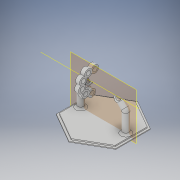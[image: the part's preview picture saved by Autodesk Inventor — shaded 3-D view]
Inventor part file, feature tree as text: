
AUTODESK INVENTOR PART (.ipt)
format: ipt  version: 2019 (Build 230136000, 136)  size: 253,952 bytes
history: native  units: mm
features: sketch x5, extrude x5, revolve x1, other x1, sweep x1, plane x1, fillet x1, mirror x1
ambient origin geometry x8: Origin, YZ Plane, XZ Plane, XY Plane, X Axis, Y Axis, Z Axis, Center Point
bodies: Solid1 (feature_tree)
feature tree (16):
  sketch  "Sketch2"  dims[d1=38.9815mm d2=180.0deg]
  revolve  "Revolution1"  Angle=180.0deg
  sketch  "Sketch3"  dims[d3=6.75mm d4=4.0mm]
  extrude  "Extrusion3"  Depth=6.75mm
  extrude  "Extrusion4"  Depth=9.599311mm
  other  "Work Axis3"
  sweep  "Sweep1"
  plane  "Work Plane1"
  sketch  "Sketch8"  dims[d14=175.0mm d15=5.0mm]
  sketch  "Sketch10"  dims[d16=5.0mm d17=0.0mm d18=2.0mm d19=0.0mm d32=90.0deg d33=0.0mm d34=0.0mm d38=11.0mm d39=4.0mm d40=60.0mm d42=34.557519mm d44=10.0mm d45=0.0mm d47=10.0mm d48=0.0mm d49=25.0mm d50=10.0mm d51=0.0mm d52=5.0mm]
  extrude  "Extrusion7"  Depth=5.0mm TaperAngle=0.0deg
  extrude  "Extrusion8"  TaperAngle=90.0deg  [1 undecoded]
  extrude  "Extrusion9"  TaperAngle=0.0deg  [1 undecoded]
  fillet  "Fillet5"  Radius=11.0mm
  mirror  "Mirror4"
  sketch  "Sketch7"  dims[d5=70.0mm d11=9.599311mm]
note: 2 required parameter values undecoded (feature->parameter linkage not recoverable at this tier; creation-order binding heuristic only, values carry confidence <= 0.55)
